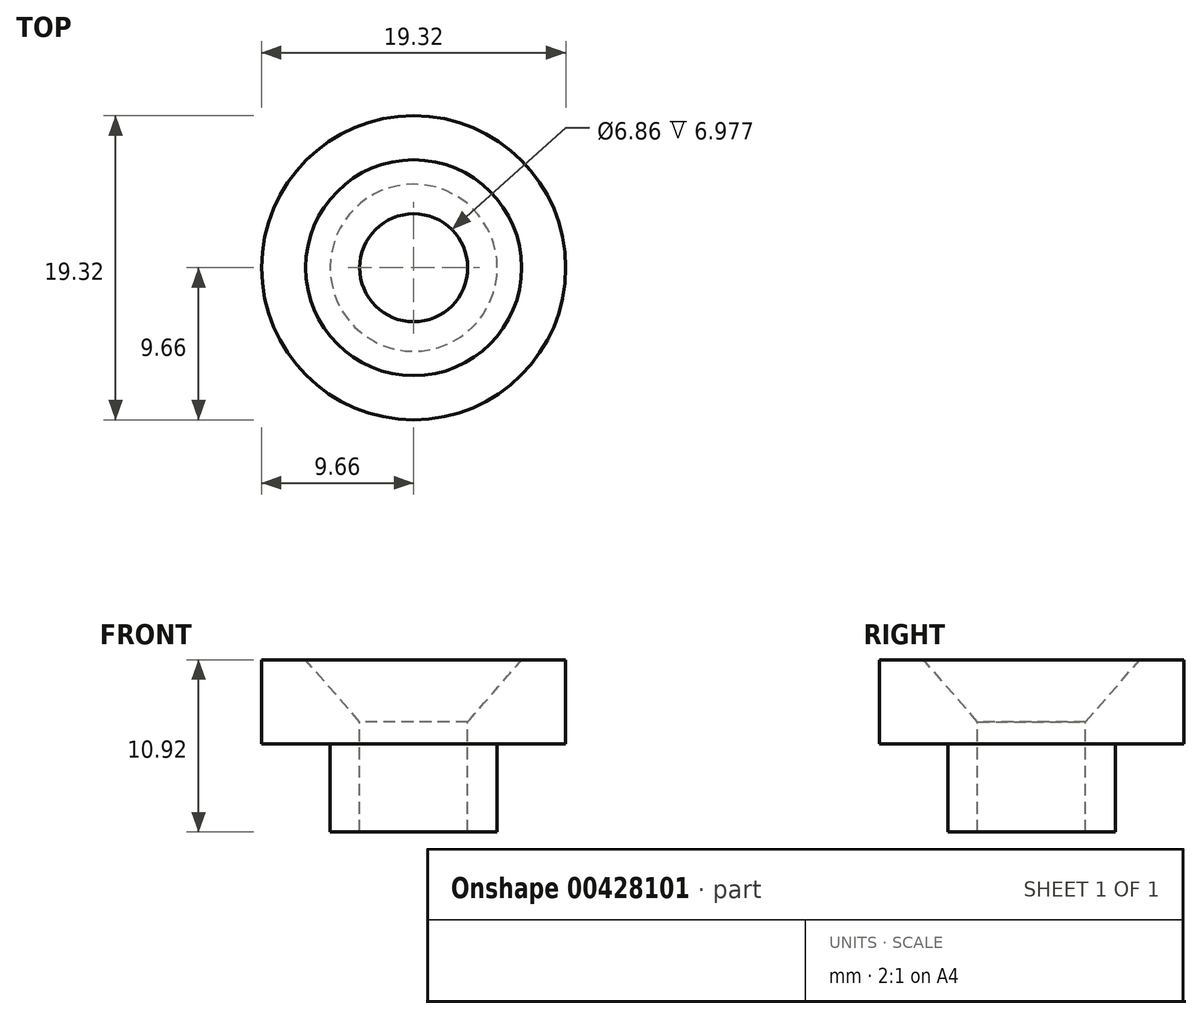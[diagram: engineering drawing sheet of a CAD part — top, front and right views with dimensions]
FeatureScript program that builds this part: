
annotation { "Feature Type Name" : "Feature", "Feature Type Description" : "" }
export const myFeature = defineFeature(function(context is Context, id is Id, definition is map)
    precondition{}
    {
        {
            var Q0;
            Q0=qCreatedBy(makeId("Top.planeOp"),FACE);
            var sketch = newSketch(context, id + "F0", { "sketchPlane" : qUnion([Q0])});
            skCircle(sketch, "E0", {"center": v(0, 0) * mm, "radius": 5.3 * mm});
            skSolve(sketch);
        }
        {
            var Q0;
            Q0 = qSketchRegion(id + "F0", true);
            extrude(context, id + "F1", {"entities" : qUnion([Q0]), "depth" : 5.6 * mm});
        }
        {
            var Q0;
            Q0=makeQuery(id+"F1.opExtrude","CAP_FACE",FACE,{"disambiguationData":[OSD([sQuery(id+"F0.wireOp",EDGE,"E0")])],"isStart":false});
            var sketch = newSketch(context, id + "F2", { "sketchPlane" : qUnion([Q0])});
            skCircle(sketch, "E1", {"center": v(0, 0) * mm, "radius": 9.66 * mm});
            skSolve(sketch);
        }
        {
            var Q0;
            Q0 = qSketchRegion(id + "F2", true);
            extrude(context, id + "F3", {"entities" : qUnion([Q0]), "operationType" : NewBodyOperationType.ADD, "depth" : 5.33 * mm});
        }
        {
            var Q0;
            Q0=makeQuery(id+"F3.opExtrude","CAP_FACE",FACE,{"disambiguationData":[OSD([sQuery(id+"F2.wireOp",EDGE,"E1")])],"isStart":false});
            var sketch = newSketch(context, id + "F4", { "sketchPlane" : qUnion([Q0])});
            skPoint(sketch, "E2", {"position": v(0, 0) * mm});
            skSolve(sketch);
        }
        {
            var Q0;
            Q0=sQuery(id+"F4.wireOp",VERTEX,"E2");
            var Q1;
            Q1=makeQuery(id+"F1.opExtrude","SWEPT_BODY",BODY,{"disambiguationData":[OSD([sQuery(id+"F0.wireOp",EDGE,"E0")])]});
            hole(context, id + "F5", {"style" : HoleStyle.C_SINK, "endStyle" : HoleEndStyle.THROUGH, "holeDiameter" : 6.86 * mm, "cSinkDiameter" : 13.72 * mm, "cSinkAngle" : 82 * degree, "isTappedThrough" : true, "tappedDepth" : 12.7 * mm, "tapClearance" : 3, "startFromSketch" : true, "locations" : qUnion([Q0]), "scope" : qUnion([Q1])});
        }
    });
